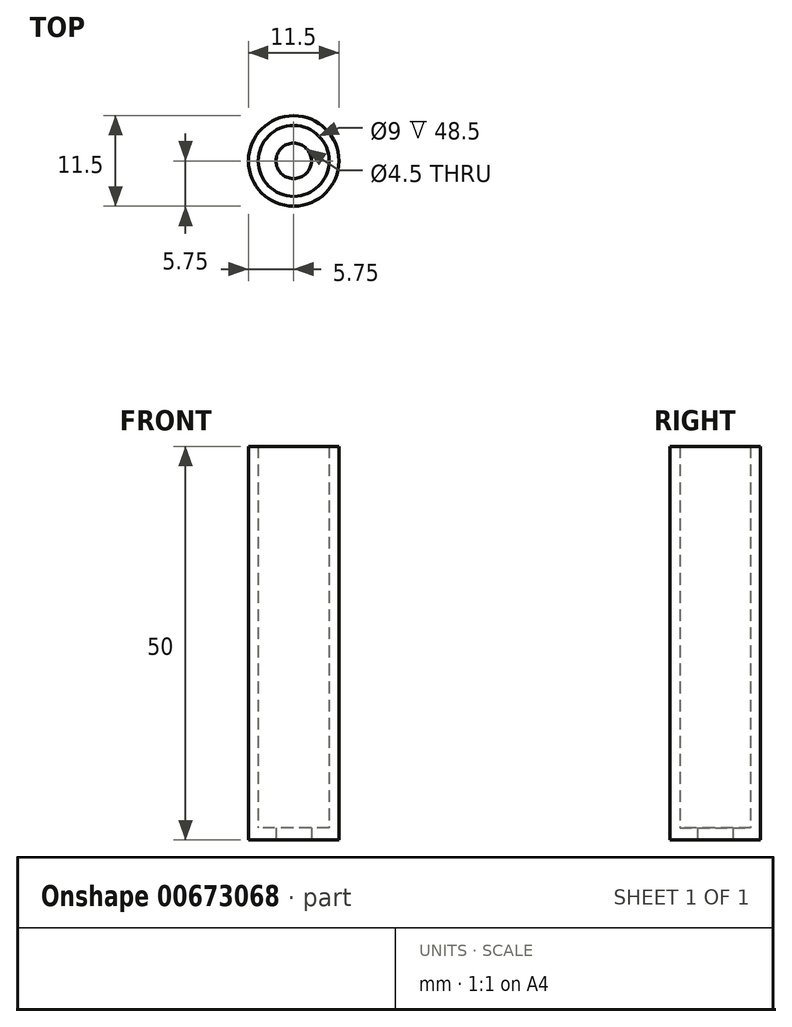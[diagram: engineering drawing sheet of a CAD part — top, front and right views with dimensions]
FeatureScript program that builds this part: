
annotation { "Feature Type Name" : "Feature", "Feature Type Description" : "" }
export const myFeature = defineFeature(function(context is Context, id is Id, definition is map)
    precondition{}
    {
        {
            var Q0;
            Q0=qCreatedBy(makeId("Top.planeOp"),FACE);
            var sketch = newSketch(context, id + "F0", { "sketchPlane" : qUnion([Q0])});
            skCircle(sketch, "E0", {"center": v(0, 0) * mm, "radius": 5.75 * mm});
            skCircle(sketch, "E1", {"center": v(0, 0) * mm, "radius": 4.5 * mm});
            skCircle(sketch, "E2", {"center": v(0, 0) * mm, "radius": 2.25 * mm});
            skSolve(sketch);
        }
        {
            var Q0;
            Q0=makeQuery(id+"F0.imprint","IMPRINT",FACE,{"disambiguationData":[TD([[makeQuery(id+"F0.imprint","IMPRINT",EDGE,{"derivedFrom":sQuery(id+"F0.wireOp",EDGE,"E0")}),1.0]])]});
            var Q1;
            Q1=sQuery(id+"F0.wireOp",EDGE,"E1");
            extrude(context, id + "F1", {"entities" : qUnion([Q0]), "surfaceEntities" : qUnion([Q1]), "depth" : 50 * mm, "offsetDistance" : 25 * mm});
        }
        {
            var Q0;
            Q0 = qSketchRegion(id + "F0", true);
            var Q1;
            Q1=makeQuery(id+"F0.imprint","IMPRINT",FACE,{"disambiguationData":[TD([[makeQuery(id+"F0.imprint","IMPRINT",EDGE,{"derivedFrom":sQuery(id+"F0.wireOp",EDGE,"E1")}),1.0]])]});
            extrude(context, id + "F2", {"entities" : qUnion([Q0, Q1]), "operationType" : NewBodyOperationType.ADD, "depth" : 1.5 * mm, "offsetDistance" : 25 * mm});
        }
    });
